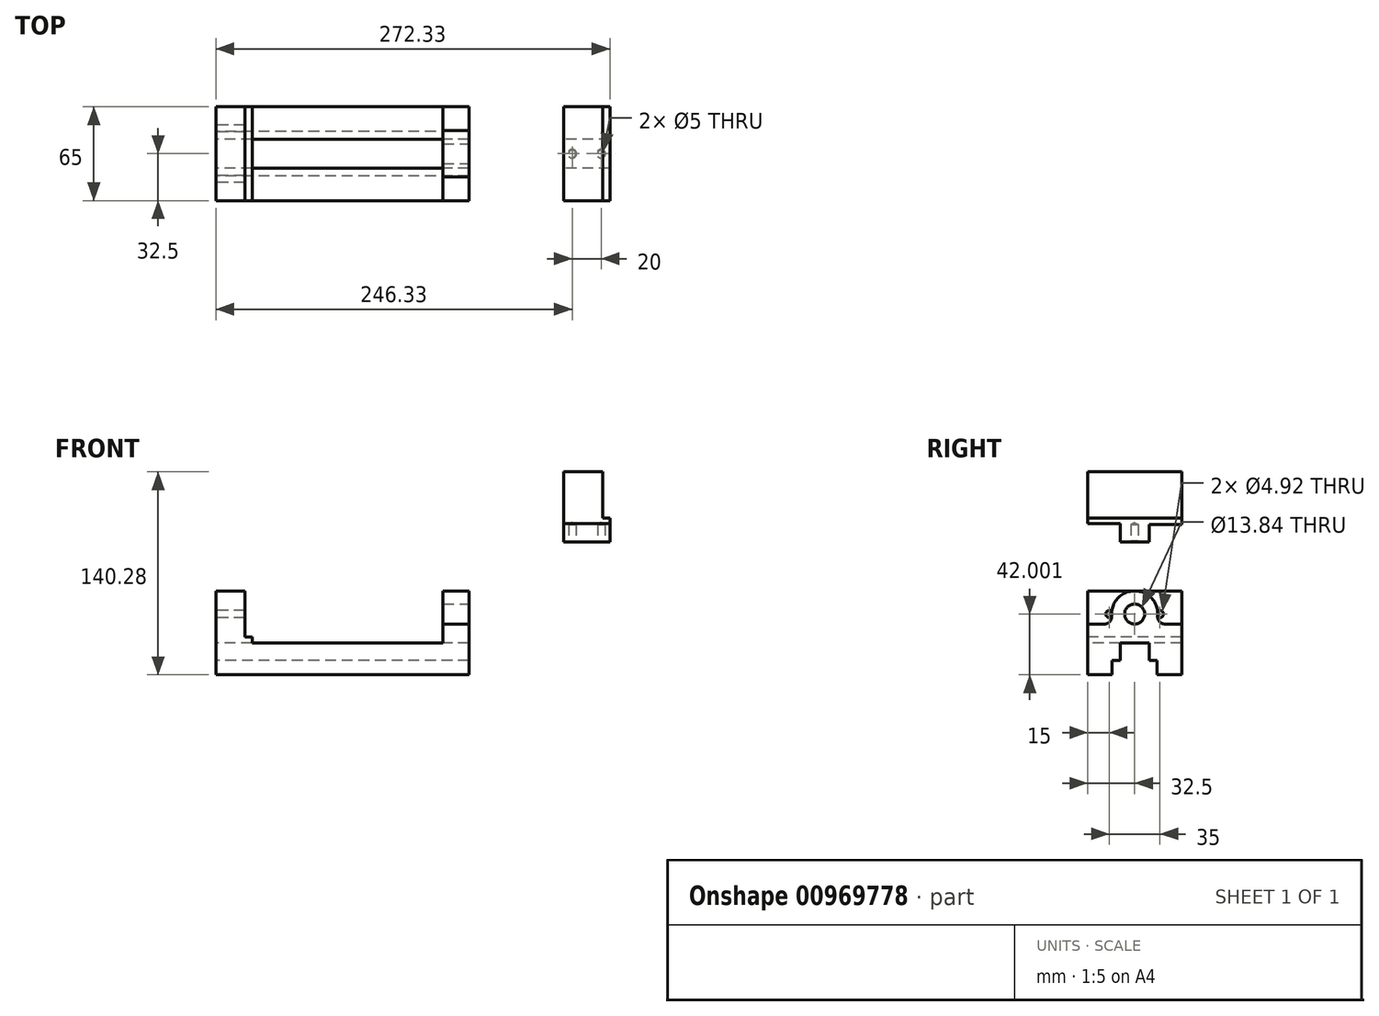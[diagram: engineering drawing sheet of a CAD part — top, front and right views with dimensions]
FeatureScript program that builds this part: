
annotation { "Feature Type Name" : "Feature", "Feature Type Description" : "" }
export const myFeature = defineFeature(function(context is Context, id is Id, definition is map)
    precondition{}
    {
        {
            var Q0;
            Q0=qCreatedBy(makeId("Front.planeOp"),FACE);
            var sketch = newSketch(context, id + "F0", { "sketchPlane" : qUnion([Q0])});
            skLineSegment(sketch, "E0.bottom", {"start": v(-90.33, -91.78) * mm, "end": v(84.67, -91.78) * mm});
            skLineSegment(sketch, "E0.top", {"start": v(-90.33, -33.78) * mm, "end": v(84.67, -33.78) * mm});
            skLineSegment(sketch, "E0.left", {"start": v(-90.33, -91.78) * mm, "end": v(-90.33, -33.78) * mm});
            skLineSegment(sketch, "E0.right", {"start": v(84.67, -91.78) * mm, "end": v(84.67, -33.78) * mm});
            skSolve(sketch);
        }
        {
            var Q0;
            Q0=makeQuery(id+"F0.imprint","IMPRINT",FACE,{"disambiguationData":[TD([[makeQuery(id+"F0.imprint","IMPRINT",EDGE,{"derivedFrom":sQuery(id+"F0.wireOp",EDGE,"E0.bottom")}),1.0]])]});
            extrude(context, id + "F1", {"entities" : qUnion([Q0]), "endBound" : BoundingType.SYMMETRIC, "depth" : 65 * mm, "offsetDistance" : 25 * mm});
        }
        {
            var Q0;
            Q0=makeQuery(id+"F1.opExtrude","SWEPT_FACE",FACE,{"disambiguationData":[OSD([sQuery(id+"F0.wireOp",EDGE,"E0.left")])]});
            var sketch = newSketch(context, id + "F2", { "sketchPlane" : qUnion([Q0])});
            skLineSegment(sketch, "E1", {"start": v(0, -91.78) * mm, "end": v(15.5, -91.78) * mm});
            skLineSegment(sketch, "E2", {"start": v(0, -91.78) * mm, "end": v(-15.5, -91.78) * mm});
            skLineSegment(sketch, "E3", {"start": v(0, -69.78) * mm, "end": v(10, -69.78) * mm});
            skLineSegment(sketch, "E4", {"start": v(0, -69.78) * mm, "end": v(-10, -69.78) * mm});
            skLineSegment(sketch, "E5", {"start": v(10, -69.78) * mm, "end": v(10, -81.78) * mm});
            skLineSegment(sketch, "E6", {"start": v(15.5, -91.78) * mm, "end": v(15.5, -81.78) * mm});
            skLineSegment(sketch, "E7", {"start": v(15.5, -81.78) * mm, "end": v(10, -81.78) * mm});
            skLineSegment(sketch, "E8", {"start": v(-10, -69.78) * mm, "end": v(-10, -81.78) * mm});
            skLineSegment(sketch, "E9", {"start": v(-15.5, -81.78) * mm, "end": v(-15.5, -91.78) * mm});
            skLineSegment(sketch, "E10", {"start": v(-10, -81.78) * mm, "end": v(-15.5, -81.78) * mm});
            skSolve(sketch);
        }
        {
            var Q0;
            Q0=makeQuery(id+"F2.imprint","IMPRINT",FACE,{"disambiguationData":[TD([[makeQuery(id+"F2.imprint","IMPRINT",EDGE,{"derivedFrom":sQuery(id+"F2.wireOp",EDGE,"E1")}),-1.0]])]});
            extrude(context, id + "F3", {"entities" : qUnion([Q0]), "operationType" : NewBodyOperationType.REMOVE, "oppositeDirection" : true, "depth" : 175 * mm, "offsetDistance" : 25 * mm});
        }
        {
            var Q0;
            Q0=makeQuery(id+"F1.opExtrude","CAP_FACE",FACE,{"disambiguationData":[OSD([sQuery(id+"F0.wireOp",EDGE,"E0.bottom"),sQuery(id+"F0.wireOp",EDGE,"E0.top"),sQuery(id+"F0.wireOp",EDGE,"E0.left"),sQuery(id+"F0.wireOp",EDGE,"E0.right")])],"isStart":false});
            var sketch = newSketch(context, id + "F4", { "sketchPlane" : qUnion([Q0])});
            skLineSegment(sketch, "E11", {"start": v(-70.33, -65.78) * mm, "end": v(-70.33, -33.78) * mm});
            skLineSegment(sketch, "E12", {"start": v(-70.33, -65.78) * mm, "end": v(-65.33, -65.78) * mm});
            skLineSegment(sketch, "E13", {"start": v(66.67, -33.78) * mm, "end": v(66.67, -69.78) * mm});
            skLineSegment(sketch, "E14", {"start": v(66.67, -69.78) * mm, "end": v(-65.33, -69.78) * mm});
            skLineSegment(sketch, "E15", {"start": v(-65.33, -69.78) * mm, "end": v(-65.33, -65.78) * mm});
            skLineSegment(sketch, "E16", {"start": v(-70.33, -33.78) * mm, "end": v(66.67, -33.78) * mm});
            skSolve(sketch);
        }
        {
            var Q0;
            Q0=makeQuery(id+"F4.imprint","IMPRINT",FACE,{"disambiguationData":[TD([[makeQuery(id+"F4.imprint","IMPRINT",EDGE,{"derivedFrom":sQuery(id+"F4.wireOp",EDGE,"E11")}),-1.0]])]});
            extrude(context, id + "F5", {"entities" : qUnion([Q0]), "operationType" : NewBodyOperationType.REMOVE, "oppositeDirection" : true, "depth" : 65 * mm, "offsetDistance" : 25 * mm});
        }
        {
            var Q0;
            Q0=makeQuery(id+"F1.opExtrude","SWEPT_FACE",FACE,{"disambiguationData":[OSD([sQuery(id+"F0.wireOp",EDGE,"E0.right")])]});
            var sketch = newSketch(context, id + "F6", { "sketchPlane" : qUnion([Q0])});
            skPoint(sketch, "E17.endSnap0", {"position": v(0, -33.78) * mm});
            skCircle(sketch, "E18", {"center": v(0, -49.78) * mm, "radius": 16 * mm});
            skCircle(sketch, "E19", {"center": v(0, -49.78) * mm, "radius": 6.92 * mm});
            skLineSegment(sketch, "E20", {"start": v(14.43, -56.7) * mm, "end": v(32.5, -56.7) * mm});
            skLineSegment(sketch, "E21", {"start": v(32.5, -33.78) * mm, "end": v(32.5, -56.7) * mm});
            skPoint(sketch, "E22.orphan", {"position": v(0, -56.7) * mm});
            skLineSegment(sketch, "E23", {"start": v(32.5, -33.78) * mm, "end": v(0, -33.78) * mm});
            skPoint(sketch, "E24.end.orphan", {"position": v(32.5, -45.24) * mm});
            skLineSegment(sketch, "E25", {"start": v(-14.43, -56.7) * mm, "end": v(-32.5, -56.7) * mm});
            skLineSegment(sketch, "E26", {"start": v(-32.5, -56.7) * mm, "end": v(-32.5, -33.78) * mm});
            skLineSegment(sketch, "E27", {"start": v(-32.5, -33.78) * mm, "end": v(0, -33.78) * mm});
            skSolve(sketch);
        }
        {
            var Q0;
            {var subQ0=sQuery(id+"F6.wireOp",EDGE,"E20");Q0=makeQuery(id+"F6.imprint","IMPRINT",FACE,{"disambiguationData":[TD([[makeQuery(id+"F6.imprint","IMPRINT",EDGE,{"derivedFrom":subQ0}),1.0]])]});}
            var Q1;
            {var subQ2=sQuery(id+"F6.wireOp",EDGE,"E25");Q1=makeQuery(id+"F6.imprint","IMPRINT",FACE,{"disambiguationData":[TD([[makeQuery(id+"F6.imprint","IMPRINT",EDGE,{"derivedFrom":subQ2}),-1.0]])]});}
            var Q2;
            Q2=makeQuery(id+"F6.imprint","IMPRINT",FACE,{"disambiguationData":[TD([[makeQuery(id+"F6.imprint","IMPRINT",EDGE,{"derivedFrom":sQuery(id+"F6.wireOp",EDGE,"E19")}),1.0]])]});
            extrude(context, id + "F7", {"entities" : qUnion([Q0, Q1, Q2]), "operationType" : NewBodyOperationType.REMOVE, "oppositeDirection" : true, "depth" : 25 * mm, "offsetDistance" : 25 * mm});
        }
        {
            var Q0;
            Q0=makeQuery(id+"F7.boolean.opBoolean","COPY",EDGE,{"derivedFrom":makeQuery(id+"F7.opExtrude","SWEPT_EDGE",EDGE,{"disambiguationData":[OSD([sQuery(id+"F6.wireOp",EDGE,"E18"),sQuery(id+"F6.wireOp",EDGE,"E25")])]})});
            var Q1;
            Q1=makeQuery(id+"F7.boolean.opBoolean","COPY",EDGE,{"derivedFrom":makeQuery(id+"F7.opExtrude","SWEPT_EDGE",EDGE,{"disambiguationData":[OSD([sQuery(id+"F6.wireOp",EDGE,"E18"),sQuery(id+"F6.wireOp",EDGE,"E20")])]})});
            var Q2;
            Q2=makeQuery(id+"F7.boolean.opBoolean","COPY",EDGE,{"derivedFrom":makeQuery(id+"F7.opExtrude","SWEPT_EDGE",EDGE,{"disambiguationData":[OSD([sQuery(id+"F0.wireOp",EDGE,"E0.right"),sQuery(id+"F6.wireOp",EDGE,"E20"),sQuery(id+"F6.wireOp",EDGE,"E21")])]})});
            var Q3;
            Q3=makeQuery(id+"F7.boolean.opBoolean","COPY",EDGE,{"derivedFrom":makeQuery(id+"F7.opExtrude","SWEPT_EDGE",EDGE,{"disambiguationData":[OSD([sQuery(id+"F0.wireOp",EDGE,"E0.right"),sQuery(id+"F6.wireOp",EDGE,"E25"),sQuery(id+"F6.wireOp",EDGE,"E26")])]})});
            fillet(context, id + "F8", {"entities" : qUnion([Q0, Q1, Q2, Q3]), "radius" : 5 * mm, "tangentPropagation" : true, "allowEdgeOverflow" : false});
        }
        {
            var Q0;
            Q0=makeQuery(id+"F1.opExtrude","SWEPT_FACE",FACE,{"disambiguationData":[OSD([sQuery(id+"F0.wireOp",EDGE,"E0.left")])]});
            var sketch = newSketch(context, id + "F9", { "sketchPlane" : qUnion([Q0])});
            skPoint(sketch, "E28.endSnap0", {"position": v(0, -33.78) * mm});
            skCircle(sketch, "E29", {"center": v(17.5, -49.78) * mm, "radius": 2.46 * mm});
            skCircle(sketch, "E30", {"center": v(-17.5, -49.78) * mm, "radius": 2.46 * mm});
            skPoint(sketch, "E28.start.orphan", {"position": v(0, -33.78) * mm});
            skPoint(sketch, "E31.orphan", {"position": v(0, -49.78) * mm});
            skSolve(sketch);
        }
        {
            var Q0;
            Q0=makeQuery(id+"F9.imprint","IMPRINT",FACE,{"disambiguationData":[TD([[makeQuery(id+"F9.imprint","IMPRINT",EDGE,{"derivedFrom":sQuery(id+"F9.wireOp",EDGE,"E29")}),1.0]])]});
            var Q1;
            Q1=makeQuery(id+"F9.imprint","IMPRINT",FACE,{"disambiguationData":[TD([[makeQuery(id+"F9.imprint","IMPRINT",EDGE,{"derivedFrom":sQuery(id+"F9.wireOp",EDGE,"E30")}),1.0]])]});
            extrude(context, id + "F10", {"entities" : qUnion([Q0, Q1]), "operationType" : NewBodyOperationType.REMOVE, "oppositeDirection" : true, "depth" : 25 * mm, "offsetDistance" : 25 * mm});
        }
        {
            var Q0;
            Q0=qCreatedBy(makeId("Right.planeOp"),FACE);
            cPlane(context, id + "F11", {"entities" : qUnion([Q0]), "cplaneType" : CPlaneType.OFFSET, "offset" : 150 * mm, "width" : 150 * mm, "height" : 150 * mm});
        }
        {
            var Q0;
            Q0=qCreatedBy(id+"F11.planeOp",FACE);
            var sketch = newSketch(context, id + "F12", { "sketchPlane" : qUnion([Q0])});
            skLineSegment(sketch, "E32", {"start": v(10, 0) * mm, "end": v(10, 12) * mm});
            skLineSegment(sketch, "E33", {"start": v(10, 12) * mm, "end": v(32.5, 12) * mm});
            skLineSegment(sketch, "E34", {"start": v(32.5, 12) * mm, "end": v(32.5, 48.5) * mm});
            skLineSegment(sketch, "E35", {"start": v(32.5, 48.5) * mm, "end": v(0, 48.5) * mm});
            skLineSegment(sketch, "E36", {"start": v(10, 0) * mm, "end": v(0, 0) * mm});
            skLineSegment(sketch, "E37", {"start": v(0, 0) * mm, "end": v(-10, 0) * mm});
            skLineSegment(sketch, "E38", {"start": v(-10, 0) * mm, "end": v(-10, 12.73) * mm});
            skLineSegment(sketch, "E39", {"start": v(-10, 12.73) * mm, "end": v(-32.5, 12.73) * mm});
            skLineSegment(sketch, "E40", {"start": v(-32.5, 12.73) * mm, "end": v(-32.5, 48.5) * mm});
            skLineSegment(sketch, "E41", {"start": v(-32.5, 48.5) * mm, "end": v(0, 48.5) * mm});
            skSolve(sketch);
        }
        {
            var Q0;
            Q0 = qSketchRegion(id + "F12", true);
            extrude(context, id + "F13", {"entities" : qUnion([Q0]), "depth" : 32 * mm, "offsetDistance" : 25 * mm});
        }
        {
            var Q0;
            Q0=makeQuery(id+"F13.opExtrude","SWEPT_FACE",FACE,{"disambiguationData":[OSD([sQuery(id+"F12.wireOp",EDGE,"E40")])]});
            var sketch = newSketch(context, id + "F14", { "sketchPlane" : qUnion([Q0])});
            skLineSegment(sketch, "E42", {"start": v(182, 48.5) * mm, "end": v(177, 48.5) * mm});
            skLineSegment(sketch, "E43", {"start": v(177, 48.5) * mm, "end": v(177, 16.5) * mm});
            skLineSegment(sketch, "E44", {"start": v(177, 16.5) * mm, "end": v(182, 16.5) * mm});
            skLineSegment(sketch, "E45", {"start": v(182, 16.5) * mm, "end": v(182, 48.5) * mm});
            skSolve(sketch);
        }
        {
            var Q0;
            Q0=makeQuery(id+"F14.imprint","IMPRINT",FACE,{"disambiguationData":[TD([[makeQuery(id+"F14.imprint","IMPRINT",EDGE,{"derivedFrom":sQuery(id+"F14.wireOp",EDGE,"E42")}),1.0]])]});
            extrude(context, id + "F15", {"entities" : qUnion([Q0]), "operationType" : NewBodyOperationType.REMOVE, "oppositeDirection" : true, "depth" : 70 * mm, "offsetDistance" : 25 * mm});
        }
        {
            var Q0;
            Q0=makeQuery(id+"F13.opExtrude","SWEPT_FACE",FACE,{"disambiguationData":[OSD([sQuery(id+"F12.wireOp",EDGE,"E36"),sQuery(id+"F12.wireOp",EDGE,"E37")])]});
            var sketch = newSketch(context, id + "F16", { "sketchPlane" : qUnion([Q0])});
            skPoint(sketch, "E46.orphan", {"position": v(182, 0) * mm});
            skPoint(sketch, "E47.end.orphan", {"position": v(150, 0) * mm});
            skPoint(sketch, "E47.start.orphan", {"position": v(166, 0) * mm});
            skLineSegment(sketch, "E48", {"start": v(166, 0) * mm, "end": v(176, 0) * mm});
            skLineSegment(sketch, "E49", {"start": v(176, 0) * mm, "end": v(166, 0) * mm});
            skLineSegment(sketch, "E50", {"start": v(156, 0) * mm, "end": v(166, 0) * mm});
            skSolve(sketch);
        }
        {
            var Q0;
            Q0=sQuery(id+"F16.wireOp",VERTEX,"E48.end");
            var Q1;
            Q1=sQuery(id+"F16.wireOp",VERTEX,"E50.start");
            var Q2;
            Q2=makeQuery(id+"F13.opExtrude","SWEPT_BODY",BODY,{"disambiguationData":[OSD([sQuery(id+"F12.wireOp",EDGE,"E32"),sQuery(id+"F12.wireOp",EDGE,"E33"),sQuery(id+"F12.wireOp",EDGE,"E34"),sQuery(id+"F12.wireOp",EDGE,"E35"),sQuery(id+"F12.wireOp",EDGE,"E36"),sQuery(id+"F12.wireOp",EDGE,"E37"),sQuery(id+"F12.wireOp",EDGE,"E38"),sQuery(id+"F12.wireOp",EDGE,"E39"),sQuery(id+"F12.wireOp",EDGE,"E40"),sQuery(id+"F12.wireOp",EDGE,"E41")])]});
            hole(context, id + "F17", {"style" : HoleStyle.C_SINK, "endStyle" : HoleEndStyle.BLIND, "holeDiameter" : 5 * mm, "cSinkDiameter" : 6 * mm, "cSinkAngle" : 1.5 * radian, "majorDiameter" : 5 * mm, "holeDepth" : 12 * mm, "isTappedThrough" : true, "tappedDepth" : 12 * mm, "tapClearance" : 3, "locations" : qUnion([Q0, Q1]), "scope" : qUnion([Q2])});
        }
    });
